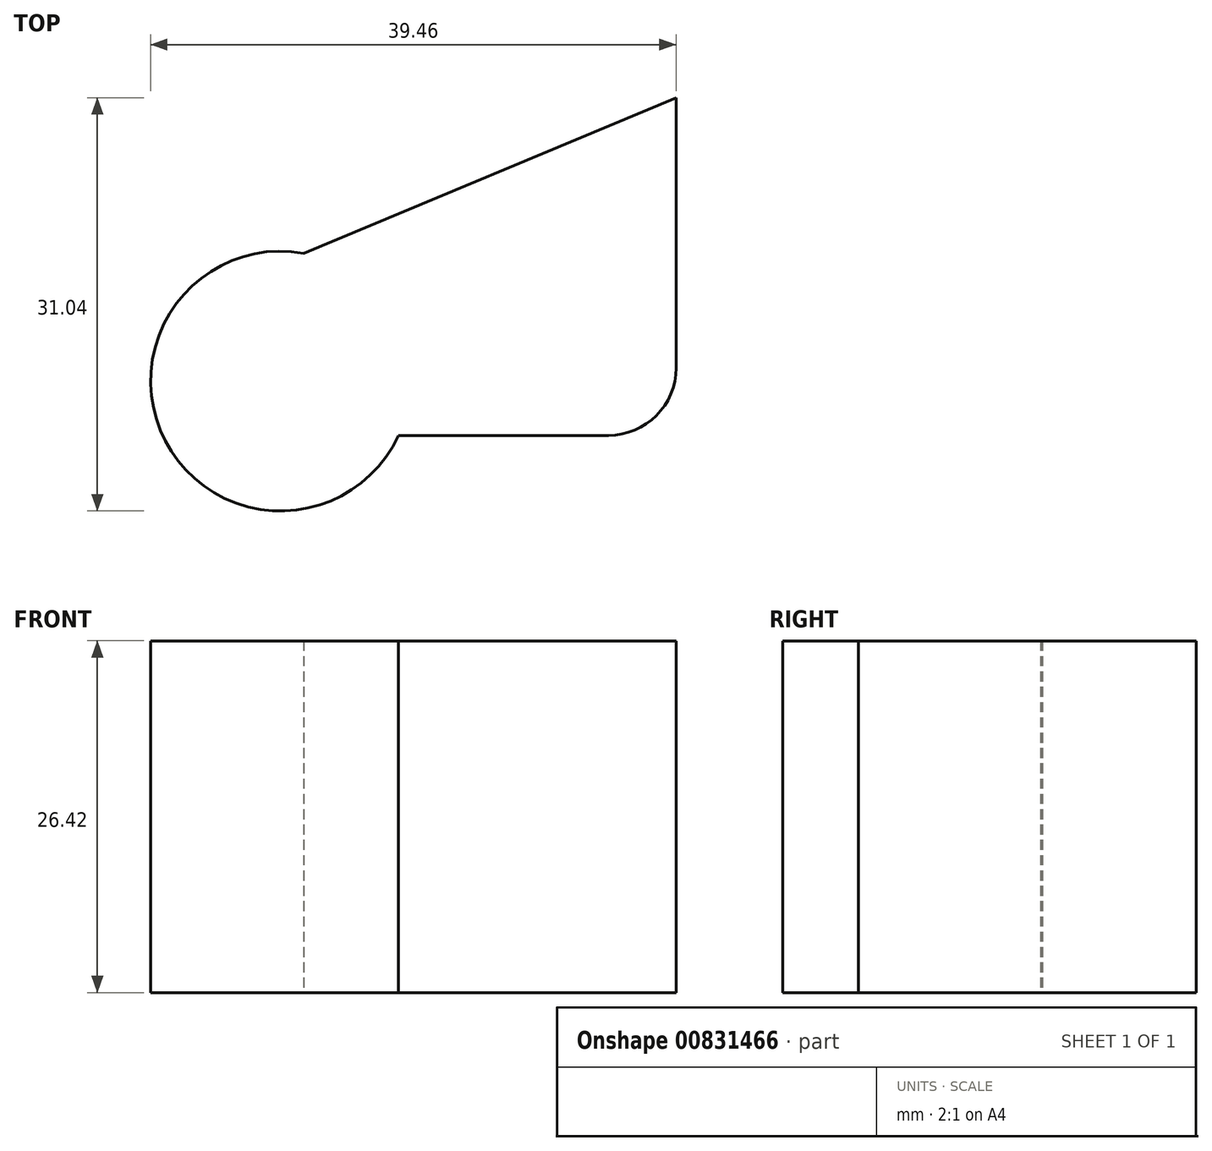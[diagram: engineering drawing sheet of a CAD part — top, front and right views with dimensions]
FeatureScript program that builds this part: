
annotation { "Feature Type Name" : "Feature", "Feature Type Description" : "" }
export const myFeature = defineFeature(function(context is Context, id is Id, definition is map)
    precondition{}
    {
        {
            var Q0;
            Q0=qCreatedBy(makeId("Top.planeOp"),FACE);
            var sketch = newSketch(context, id + "F0", { "sketchPlane" : qUnion([Q0])});
            skArc(sketch, "E0", {"start": v(-21.16, 21.94) * mm, "mid": v(-31.53, 7.83) * mm, "end": v(-14.02, 8.26) * mm});
            skPoint(sketch, "E0.first.point", {"position": v(-32.62, 12.94) * mm});
            skPoint(sketch, "E0.second.point", {"position": v(-21.16, 21.94) * mm});
            skPoint(sketch, "E0.third.point", {"position": v(-14.02, 8.26) * mm});
            skLineSegment(sketch, "E1", {"start": v(-21.16, 21.94) * mm, "end": v(6.82, 33.62) * mm});
            skLineSegment(sketch, "E2", {"start": v(6.82, 33.62) * mm, "end": v(6.82, 21.94) * mm});
            skLineSegment(sketch, "E3", {"start": v(6.82, 21.94) * mm, "end": v(6.82, 13.34) * mm});
            skLineSegment(sketch, "E4", {"start": v(1.74, 8.26) * mm, "end": v(-14.02, 8.26) * mm});
            skPoint(sketch, "E5.visualSharp", {"position": v(6.82, 8.26) * mm});
            skArc(sketch, "E5.filletArc", {"start": v(1.74, 8.26) * mm, "mid": v(5.33, 9.74) * mm, "end": v(6.82, 13.34) * mm});
            skSolve(sketch);
        }
        {
            var Q0;
            Q0=makeQuery(id+"F0.imprint","IMPRINT",FACE,{"disambiguationData":[TD([[makeQuery(id+"F0.imprint","IMPRINT",EDGE,{"derivedFrom":sQuery(id+"F0.wireOp",EDGE,"E0")}),1.0]])]});
            extrude(context, id + "F1", {"entities" : qUnion([Q0]), "depth" : 26.42 * mm, "offsetDistance" : 25.4 * mm});
        }
    });
